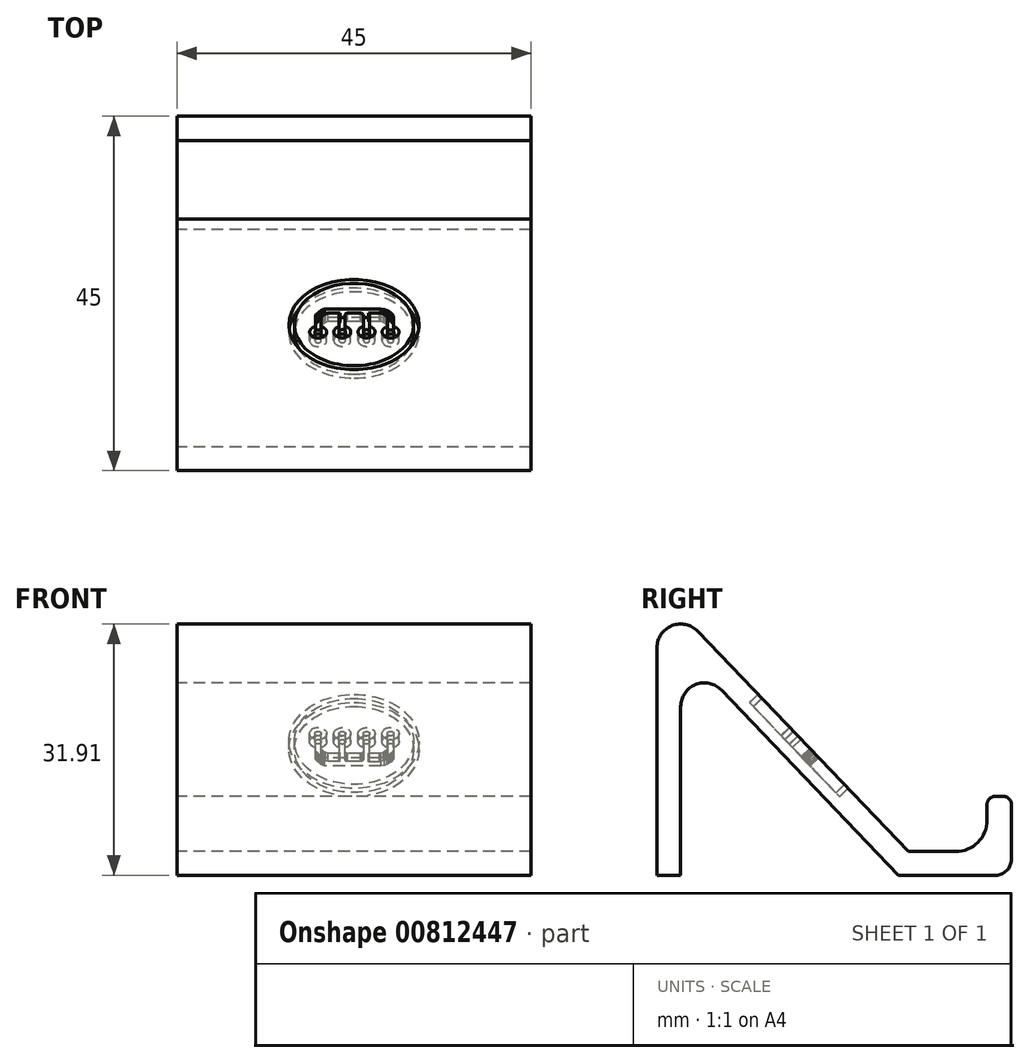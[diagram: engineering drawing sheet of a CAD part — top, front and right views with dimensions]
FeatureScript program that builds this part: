
annotation { "Feature Type Name" : "Feature", "Feature Type Description" : "" }
export const myFeature = defineFeature(function(context is Context, id is Id, definition is map)
    precondition{}
    {
        {
            var Q0;
            Q0=qCreatedBy(makeId("Right.planeOp"),FACE);
            var sketch = newSketch(context, id + "F0", { "sketchPlane" : qUnion([Q0])});
            skLineSegment(sketch, "E0", {"start": v(0, 0) * mm, "end": v(-22.47, 23.5) * mm});
            skLineSegment(sketch, "E1", {"start": v(-27.64, 21.43) * mm, "end": v(-27.64, 0) * mm});
            skLineSegment(sketch, "E2", {"start": v(0, 0) * mm, "end": v(12.36, 0) * mm});
            skLineSegment(sketch, "E3.0", {"start": v(-30.64, 28.91) * mm, "end": v(-30.64, 0) * mm});
            skLineSegment(sketch, "E3.1", {"start": v(1.28, 3) * mm, "end": v(-25.47, 30.99) * mm});
            skLineSegment(sketch, "E3.2", {"start": v(1.28, 3) * mm, "end": v(7.28, 3) * mm});
            skLineSegment(sketch, "E4", {"start": v(-27.64, 0) * mm, "end": v(-30.64, 0) * mm});
            skPoint(sketch, "E5.visualSharp", {"position": v(-27.64, 28.91) * mm});
            skArc(sketch, "E5.filletArc", {"start": v(-22.47, 23.5) * mm, "mid": v(-25.76, 24.22) * mm, "end": v(-27.64, 21.43) * mm});
            skPoint(sketch, "E6.visualSharp", {"position": v(-30.64, 36.4) * mm});
            skArc(sketch, "E6.filletArc", {"start": v(-25.47, 30.99) * mm, "mid": v(-28.76, 31.7) * mm, "end": v(-30.64, 28.91) * mm});
            skLineSegment(sketch, "E7", {"start": v(14.36, 2) * mm, "end": v(14.36, 7) * mm});
            skLineSegment(sketch, "E8.3", {"start": v(11.28, 7) * mm, "end": v(11.28, 7) * mm});
            skLineSegment(sketch, "E9", {"start": v(14.36, 7) * mm, "end": v(14.36, 9) * mm});
            skLineSegment(sketch, "E10", {"start": v(11.28, 7) * mm, "end": v(11.28, 9) * mm});
            skLineSegment(sketch, "E11", {"start": v(13.36, 10) * mm, "end": v(12.28, 10) * mm});
            skPoint(sketch, "E12.visualSharp", {"position": v(14.36, 0) * mm});
            skArc(sketch, "E12.filletArc", {"start": v(12.36, 0) * mm, "mid": v(13.78, 0.59) * mm, "end": v(14.36, 2) * mm});
            skPoint(sketch, "E13.visualSharp", {"position": v(14.36, 10) * mm});
            skArc(sketch, "E13.filletArc", {"start": v(14.36, 9) * mm, "mid": v(14.07, 9.7) * mm, "end": v(13.36, 10) * mm});
            skPoint(sketch, "E14.visualSharp", {"position": v(11.28, 10) * mm});
            skArc(sketch, "E14.filletArc", {"start": v(12.28, 10) * mm, "mid": v(11.58, 9.7) * mm, "end": v(11.28, 9) * mm});
            skPoint(sketch, "E15.orphan", {"position": v(6.46, 0) * mm});
            skPoint(sketch, "E16.visualSharp", {"position": v(11.28, 3) * mm});
            skArc(sketch, "E16.filletArc", {"start": v(7.28, 3) * mm, "mid": v(10.11, 4.17) * mm, "end": v(11.28, 7) * mm});
            skSolve(sketch);
        }
        {
            var Q0;
            Q0=makeQuery(id+"F0.imprint","IMPRINT",FACE,{"disambiguationData":[TD([[makeQuery(id+"F0.imprint","IMPRINT",EDGE,{"derivedFrom":sQuery(id+"F0.wireOp",EDGE,"E0")}),-1.0]])]});
            extrude(context, id + "F1", {"entities" : qUnion([Q0]), "depth" : 45 * mm, "offsetDistance" : 25 * mm});
        }
        {
            var Q0;
            Q0=makeQuery(id+"F1.opExtrude","SWEPT_FACE",FACE,{"disambiguationData":[OSD([sQuery(id+"F0.wireOp",EDGE,"E3.1")])]});
            var sketch = newSketch(context, id + "F2", { "sketchPlane" : qUnion([Q0])});
            skCircle(sketch, "E17", {"center": v(-22.5, 20.64) * mm, "radius": 7.57 * mm});
            skPoint(sketch, "E18", {"position": v(-22.5, 40) * mm});
            skPoint(sketch, "E19", {"position": v(0, 20.64) * mm});
            skCircle(sketch, "E20", {"center": v(-22.5, 20.64) * mm, "radius": 8.27 * mm});
            skCircle(sketch, "E21", {"center": v(-27.15, 22.02) * mm, "radius": 0.4 * mm});
            skArc(sketch, "E22", {"start": v(-26.75, 21.02) * mm, "mid": v(-27.16, 23.1) * mm, "end": v(-27.52, 21) * mm});
            skCircle(sketch, "E23", {"center": v(-24.1, 22) * mm, "radius": 0.4 * mm});
            skArc(sketch, "E24", {"start": v(-23.71, 21) * mm, "mid": v(-24.09, 23.08) * mm, "end": v(-24.5, 21) * mm});
            skCircle(sketch, "E25", {"center": v(-21.01, 22) * mm, "radius": 0.4 * mm});
            skArc(sketch, "E26", {"start": v(-20.58, 21.01) * mm, "mid": v(-21.05, 23.08) * mm, "end": v(-21.37, 20.99) * mm});
            skCircle(sketch, "E27", {"center": v(-17.94, 22.02) * mm, "radius": 0.4 * mm});
            skArc(sketch, "E28", {"start": v(-17.6, 21) * mm, "mid": v(-17.91, 23.1) * mm, "end": v(-18.34, 21.02) * mm});
            skLineSegment(sketch, "E29", {"start": v(-27.52, 21) * mm, "end": v(-27.52, 19.1) * mm});
            skLineSegment(sketch, "E30", {"start": v(-27.52, 19.1) * mm, "end": v(-27.38, 18.83) * mm});
            skLineSegment(sketch, "E31", {"start": v(-27.38, 18.83) * mm, "end": v(-27.18, 18.52) * mm});
            skLineSegment(sketch, "E32", {"start": v(-27.18, 18.52) * mm, "end": v(-26.96, 18.28) * mm});
            skLineSegment(sketch, "E33", {"start": v(-26.96, 18.28) * mm, "end": v(-26.69, 18.05) * mm});
            skLineSegment(sketch, "E34", {"start": v(-26.69, 18.05) * mm, "end": v(-26.36, 17.9) * mm});
            skLineSegment(sketch, "E35", {"start": v(-26.36, 17.9) * mm, "end": v(-25.93, 17.79) * mm});
            skLineSegment(sketch, "E36", {"start": v(-25.93, 17.79) * mm, "end": v(-18.78, 17.79) * mm});
            skLineSegment(sketch, "E37", {"start": v(-18.78, 17.79) * mm, "end": v(-18.55, 17.9) * mm});
            skLineSegment(sketch, "E38", {"start": v(-18.55, 17.9) * mm, "end": v(-18.34, 18.05) * mm});
            skLineSegment(sketch, "E39", {"start": v(-18.34, 18.05) * mm, "end": v(-18.1, 18.28) * mm});
            skLineSegment(sketch, "E40", {"start": v(-18.1, 18.28) * mm, "end": v(-17.9, 18.52) * mm});
            skLineSegment(sketch, "E41", {"start": v(-17.9, 18.52) * mm, "end": v(-17.7, 18.83) * mm});
            skLineSegment(sketch, "E42", {"start": v(-17.7, 18.83) * mm, "end": v(-17.6, 19.1) * mm});
            skLineSegment(sketch, "E43", {"start": v(-17.6, 19.1) * mm, "end": v(-17.6, 21) * mm});
            skLineSegment(sketch, "E44", {"start": v(-26.75, 21.02) * mm, "end": v(-26.75, 19.3) * mm});
            skLineSegment(sketch, "E45", {"start": v(-26.75, 19.3) * mm, "end": v(-26.6, 19.05) * mm});
            skLineSegment(sketch, "E46", {"start": v(-26.6, 19.05) * mm, "end": v(-26.43, 18.86) * mm});
            skLineSegment(sketch, "E47", {"start": v(-26.43, 18.86) * mm, "end": v(-26.22, 18.7) * mm});
            skLineSegment(sketch, "E48", {"start": v(-26.22, 18.7) * mm, "end": v(-25.95, 18.56) * mm});
            skLineSegment(sketch, "E49", {"start": v(-25.95, 18.56) * mm, "end": v(-25.72, 18.52) * mm});
            skLineSegment(sketch, "E50", {"start": v(-25.72, 18.52) * mm, "end": v(-24.34, 18.52) * mm});
            skLineSegment(sketch, "E51", {"start": v(-24.34, 18.52) * mm, "end": v(-24.49, 18.65) * mm});
            skLineSegment(sketch, "E52", {"start": v(-24.49, 18.65) * mm, "end": v(-24.5, 18.8) * mm});
            skLineSegment(sketch, "E53", {"start": v(-24.5, 18.8) * mm, "end": v(-24.5, 21) * mm});
            skLineSegment(sketch, "E54", {"start": v(-23.71, 21) * mm, "end": v(-23.71, 18.8) * mm});
            skLineSegment(sketch, "E55", {"start": v(-23.71, 18.8) * mm, "end": v(-23.61, 18.67) * mm});
            skLineSegment(sketch, "E56", {"start": v(-23.61, 18.67) * mm, "end": v(-23.47, 18.57) * mm});
            skLineSegment(sketch, "E57", {"start": v(-23.47, 18.57) * mm, "end": v(-23.33, 18.53) * mm});
            skLineSegment(sketch, "E58", {"start": v(-23.33, 18.53) * mm, "end": v(-21.65, 18.53) * mm});
            skLineSegment(sketch, "E59", {"start": v(-21.65, 18.53) * mm, "end": v(-21.48, 18.6) * mm});
            skLineSegment(sketch, "E60", {"start": v(-21.48, 18.6) * mm, "end": v(-21.41, 18.69) * mm});
            skLineSegment(sketch, "E61", {"start": v(-21.41, 18.69) * mm, "end": v(-21.37, 18.84) * mm});
            skLineSegment(sketch, "E62", {"start": v(-21.37, 18.84) * mm, "end": v(-21.37, 20.99) * mm});
            skLineSegment(sketch, "E63", {"start": v(-20.58, 21.01) * mm, "end": v(-20.58, 18.82) * mm});
            skLineSegment(sketch, "E64", {"start": v(-20.58, 18.82) * mm, "end": v(-20.66, 18.67) * mm});
            skLineSegment(sketch, "E65", {"start": v(-20.66, 18.67) * mm, "end": v(-20.72, 18.53) * mm});
            skLineSegment(sketch, "E66", {"start": v(-20.72, 18.53) * mm, "end": v(-19.2, 18.53) * mm});
            skLineSegment(sketch, "E67", {"start": v(-19.2, 18.53) * mm, "end": v(-18.86, 18.69) * mm});
            skLineSegment(sketch, "E68", {"start": v(-18.86, 18.69) * mm, "end": v(-18.7, 18.84) * mm});
            skLineSegment(sketch, "E69", {"start": v(-18.7, 18.84) * mm, "end": v(-18.56, 19.01) * mm});
            skLineSegment(sketch, "E70", {"start": v(-18.56, 19.01) * mm, "end": v(-18.4, 19.25) * mm});
            skLineSegment(sketch, "E71", {"start": v(-18.4, 19.25) * mm, "end": v(-18.34, 19.42) * mm});
            skLineSegment(sketch, "E72", {"start": v(-18.34, 19.42) * mm, "end": v(-18.34, 21.02) * mm});
            skSolve(sketch);
        }
        {
            var Q0;
            Q0 = qSketchRegion(id + "F2", true);
            var Q1;
            Q1=makeQuery(id+"F2.imprint","IMPRINT",FACE,{"disambiguationData":[TD([[makeQuery(id+"F2.imprint","IMPRINT",EDGE,{"derivedFrom":sQuery(id+"F2.wireOp",EDGE,"E21")}),-1.0]])]});
            extrude(context, id + "F3", {"entities" : qUnion([Q0, Q1]), "operationType" : NewBodyOperationType.REMOVE, "oppositeDirection" : true, "depth" : 1.5 * mm, "offsetDistance" : 25 * mm});
        }
    });
